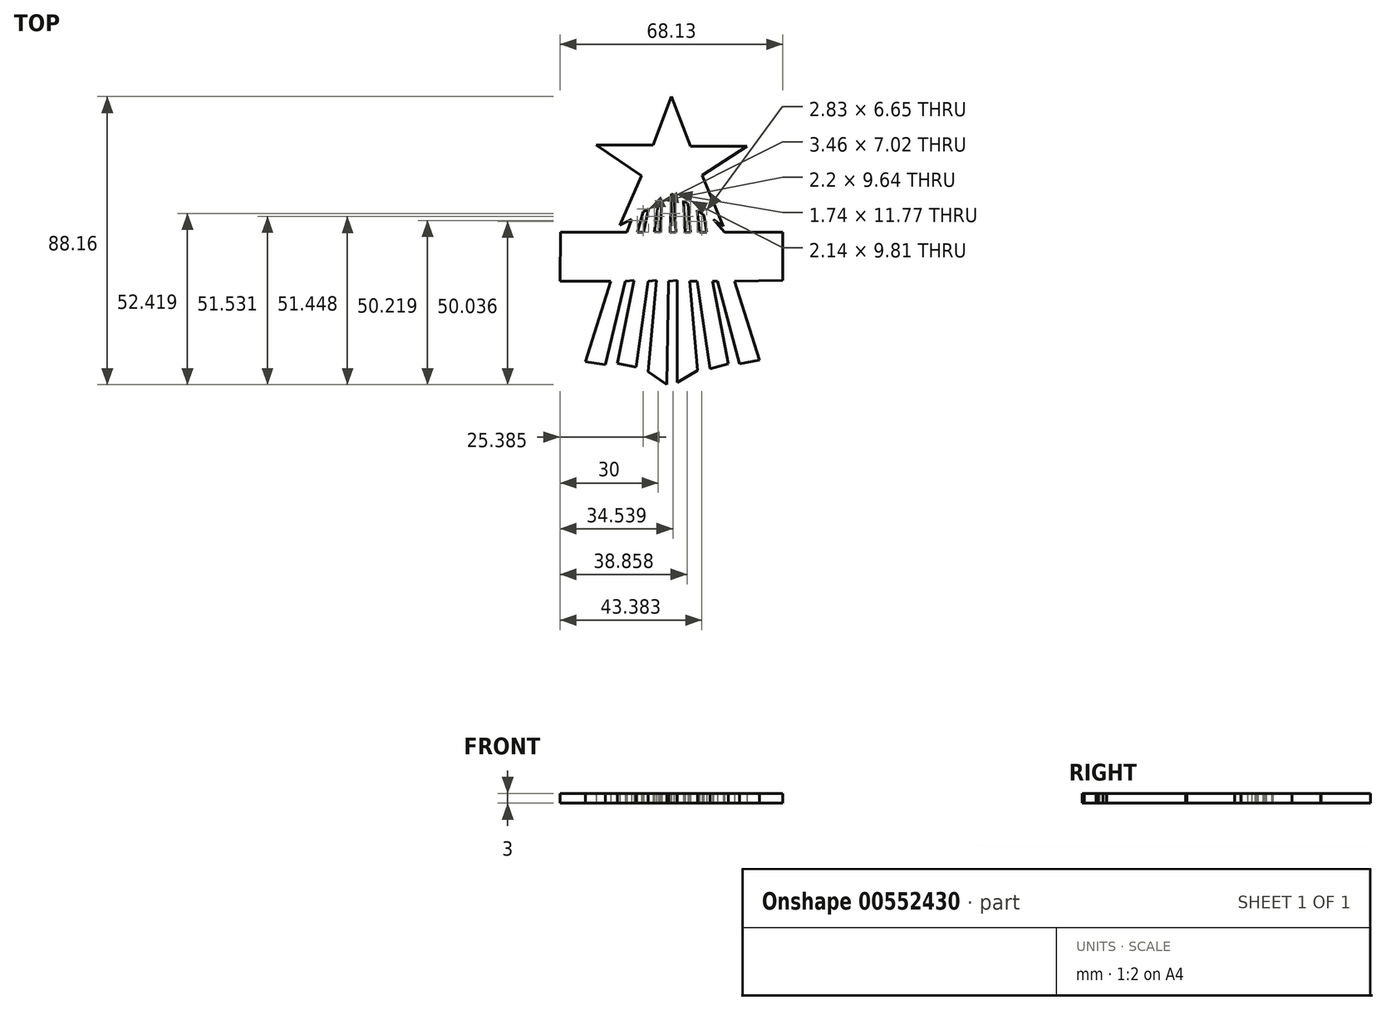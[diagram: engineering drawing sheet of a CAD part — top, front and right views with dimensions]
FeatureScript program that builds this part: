
annotation { "Feature Type Name" : "Feature", "Feature Type Description" : "" }
export const myFeature = defineFeature(function(context is Context, id is Id, definition is map)
    precondition{}
    {
        {
            var Q0;
            Q0=qCreatedBy(makeId("Top.planeOp"),FACE);
            var sketch = newSketch(context, id + "F0", { "sketchPlane" : qUnion([Q0])});
            skLineSegment(sketch, "E0", {"start": v(-118.77, 15.2) * mm, "end": v(-124.28, 0.4) * mm});
            skLineSegment(sketch, "E1", {"start": v(-124.28, 0.4) * mm, "end": v(-141.78, 0.4) * mm});
            skLineSegment(sketch, "E2", {"start": v(-141.78, 0.4) * mm, "end": v(-127.85, -9.03) * mm});
            skLineSegment(sketch, "E3", {"start": v(-127.85, -9.03) * mm, "end": v(-134.44, -24.16) * mm});
            skLineSegment(sketch, "E4", {"start": v(-134.44, -24.16) * mm, "end": v(-130.94, -22.36) * mm});
            skLineSegment(sketch, "E5", {"start": v(-130.94, -22.36) * mm, "end": v(-132.36, -26.25) * mm});
            skLineSegment(sketch, "E6", {"start": v(-132.36, -26.25) * mm, "end": v(-152.68, -26.25) * mm});
            skLineSegment(sketch, "E7", {"start": v(-84.72, -26.25) * mm, "end": v(-102.5, -26.25) * mm});
            skLineSegment(sketch, "E8", {"start": v(-102.5, -26.25) * mm, "end": v(-105.95, -22.36) * mm});
            skLineSegment(sketch, "E9", {"start": v(-105.95, -22.36) * mm, "end": v(-102.94, -24.45) * mm});
            skLineSegment(sketch, "E10", {"start": v(-102.94, -24.45) * mm, "end": v(-109.31, -8.84) * mm});
            skLineSegment(sketch, "E11", {"start": v(-109.31, -8.84) * mm, "end": v(-95.6, 0) * mm});
            skLineSegment(sketch, "E12", {"start": v(-95.6, 0) * mm, "end": v(-112.93, 0) * mm});
            skLineSegment(sketch, "E13", {"start": v(-112.93, 0) * mm, "end": v(-118.77, 15.2) * mm});
            skLineSegment(sketch, "E14", {"start": v(-110.83, -19.6) * mm, "end": v(-110.17, -26.25) * mm});
            skLineSegment(sketch, "E15", {"start": v(-110.17, -26.25) * mm, "end": v(-108, -26.25) * mm});
            skLineSegment(sketch, "E16", {"start": v(-108, -26.25) * mm, "end": v(-108.83, -21.08) * mm});
            skLineSegment(sketch, "E17", {"start": v(-108.83, -21.08) * mm, "end": v(-110.83, -19.6) * mm});
            skLineSegment(sketch, "E18", {"start": v(-115.01, -16.6) * mm, "end": v(-113.73, -17.7) * mm});
            skLineSegment(sketch, "E19", {"start": v(-113.73, -17.7) * mm, "end": v(-112.87, -26.25) * mm});
            skLineSegment(sketch, "E20", {"start": v(-112.87, -26.25) * mm, "end": v(-114.53, -26.42) * mm});
            skLineSegment(sketch, "E21", {"start": v(-114.53, -26.42) * mm, "end": v(-115.01, -16.6) * mm});
            skLineSegment(sketch, "E22", {"start": v(-118.77, -14.66) * mm, "end": v(-117.95, -14.96) * mm});
            skLineSegment(sketch, "E23", {"start": v(-117.95, -14.96) * mm, "end": v(-117.4, -26.25) * mm});
            skLineSegment(sketch, "E24", {"start": v(-117.4, -26.25) * mm, "end": v(-119.13, -26.42) * mm});
            skLineSegment(sketch, "E25", {"start": v(-119.13, -26.42) * mm, "end": v(-118.77, -14.66) * mm});
            skLineSegment(sketch, "E26", {"start": v(-122.72, -17.13) * mm, "end": v(-121.7, -16.6) * mm});
            skLineSegment(sketch, "E27", {"start": v(-121.7, -16.6) * mm, "end": v(-122.2, -26.25) * mm});
            skLineSegment(sketch, "E28", {"start": v(-122.2, -26.25) * mm, "end": v(-123.9, -26.16) * mm});
            skLineSegment(sketch, "E29", {"start": v(-123.9, -26.16) * mm, "end": v(-122.72, -17.13) * mm});
            skLineSegment(sketch, "E30", {"start": v(-127.43, -20.13) * mm, "end": v(-125.69, -19.23) * mm});
            skLineSegment(sketch, "E31", {"start": v(-125.69, -19.23) * mm, "end": v(-127.29, -26.25) * mm});
            skLineSegment(sketch, "E32", {"start": v(-127.29, -26.25) * mm, "end": v(-129.14, -26.25) * mm});
            skLineSegment(sketch, "E33", {"start": v(-129.14, -26.25) * mm, "end": v(-127.43, -20.13) * mm});
            skLineSegment(sketch, "E34", {"start": v(-152.8, -41.23) * mm, "end": v(-137.32, -41.23) * mm});
            skLineSegment(sketch, "E35", {"start": v(-137.32, -41.23) * mm, "end": v(-145, -65.86) * mm});
            skLineSegment(sketch, "E36", {"start": v(-132.88, -41.23) * mm, "end": v(-130.2, -40.96) * mm});
            skLineSegment(sketch, "E37", {"start": v(-130.2, -40.96) * mm, "end": v(-135.3, -66.4) * mm});
            skLineSegment(sketch, "E38", {"start": v(-135.3, -66.4) * mm, "end": v(-138.93, -66.76) * mm});
            skLineSegment(sketch, "E39", {"start": v(-138.93, -66.76) * mm, "end": v(-132.88, -41.23) * mm});
            skLineSegment(sketch, "E40", {"start": v(-125.89, -41.23) * mm, "end": v(-123.3, -40.97) * mm});
            skLineSegment(sketch, "E41", {"start": v(-123.3, -40.97) * mm, "end": v(-125.89, -68.95) * mm});
            skLineSegment(sketch, "E42", {"start": v(-125.89, -68.95) * mm, "end": v(-129.57, -67.6) * mm});
            skLineSegment(sketch, "E43", {"start": v(-129.57, -67.6) * mm, "end": v(-125.89, -41.23) * mm});
            skLineSegment(sketch, "E44", {"start": v(-119.62, -41.23) * mm, "end": v(-116.96, -40.97) * mm});
            skLineSegment(sketch, "E45", {"start": v(-116.96, -40.97) * mm, "end": v(-116.96, -72.32) * mm});
            skLineSegment(sketch, "E46", {"start": v(-116.96, -72.32) * mm, "end": v(-118.55, -74.54) * mm});
            skLineSegment(sketch, "E47", {"start": v(-118.55, -74.54) * mm, "end": v(-120.1, -72.96) * mm});
            skLineSegment(sketch, "E48", {"start": v(-120.1, -72.96) * mm, "end": v(-119.62, -41.23) * mm});
            skLineSegment(sketch, "E49", {"start": v(-113.19, -41.23) * mm, "end": v(-110.9, -41.23) * mm});
            skLineSegment(sketch, "E50", {"start": v(-110.9, -41.23) * mm, "end": v(-107, -68.03) * mm});
            skLineSegment(sketch, "E51", {"start": v(-107, -68.03) * mm, "end": v(-110.74, -68.57) * mm});
            skLineSegment(sketch, "E52", {"start": v(-110.74, -68.57) * mm, "end": v(-113.19, -41.23) * mm});
            skLineSegment(sketch, "E53", {"start": v(-106.15, -41.23) * mm, "end": v(-104.62, -41.23) * mm});
            skLineSegment(sketch, "E54", {"start": v(-104.62, -41.23) * mm, "end": v(-97.87, -66.6) * mm});
            skLineSegment(sketch, "E55", {"start": v(-97.87, -66.6) * mm, "end": v(-101.3, -66.6) * mm});
            skLineSegment(sketch, "E56", {"start": v(-101.3, -66.6) * mm, "end": v(-106.15, -41.23) * mm});
            skLineSegment(sketch, "E57", {"start": v(-99.48, -41.23) * mm, "end": v(-91.78, -65.37) * mm});
            skLineSegment(sketch, "E58", {"start": v(-84.67, -40.97) * mm, "end": v(-99.48, -41.23) * mm});
            skLineSegment(sketch, "E59", {"start": v(-91.78, -65.37) * mm, "end": v(-97.87, -66.6) * mm});
            skLineSegment(sketch, "E60", {"start": v(-101.3, -66.6) * mm, "end": v(-107, -68.03) * mm});
            skLineSegment(sketch, "E61", {"start": v(-110.74, -68.57) * mm, "end": v(-116.96, -72.32) * mm});
            skLineSegment(sketch, "E62", {"start": v(-120.1, -72.96) * mm, "end": v(-125.89, -68.95) * mm});
            skLineSegment(sketch, "E63", {"start": v(-129.57, -67.6) * mm, "end": v(-135.3, -66.4) * mm});
            skLineSegment(sketch, "E64", {"start": v(-138.93, -66.76) * mm, "end": v(-145, -65.86) * mm});
            skLineSegment(sketch, "E65", {"start": v(-84.72, -26.25) * mm, "end": v(-84.67, -40.97) * mm});
            skLineSegment(sketch, "E66", {"start": v(-152.68, -26.25) * mm, "end": v(-152.8, -41.23) * mm});
            skSolve(sketch);
        }
        {
            var Q0;
            Q0=makeQuery(id+"F0.imprint","IMPRINT",FACE,{"disambiguationData":[TD([[makeQuery(id+"F0.imprint","IMPRINT",EDGE,{"derivedFrom":sQuery(id+"F0.wireOp",EDGE,"E7")}),1.0]])]});
            var Q1;
            {var subQ0=sQuery(id+"F0.wireOp",EDGE,"E1");Q1=makeQuery(id+"F0.imprint","IMPRINT",FACE,{"disambiguationData":[TD([[makeQuery(id+"F0.imprint","IMPRINT",EDGE,{"derivedFrom":subQ0}),1.0]])]});}
            extrude(context, id + "F1", {"entities" : qUnion([Q0, Q1]), "depth" : 3 * mm, "offsetDistance" : 25.4 * mm});
        }
    });
